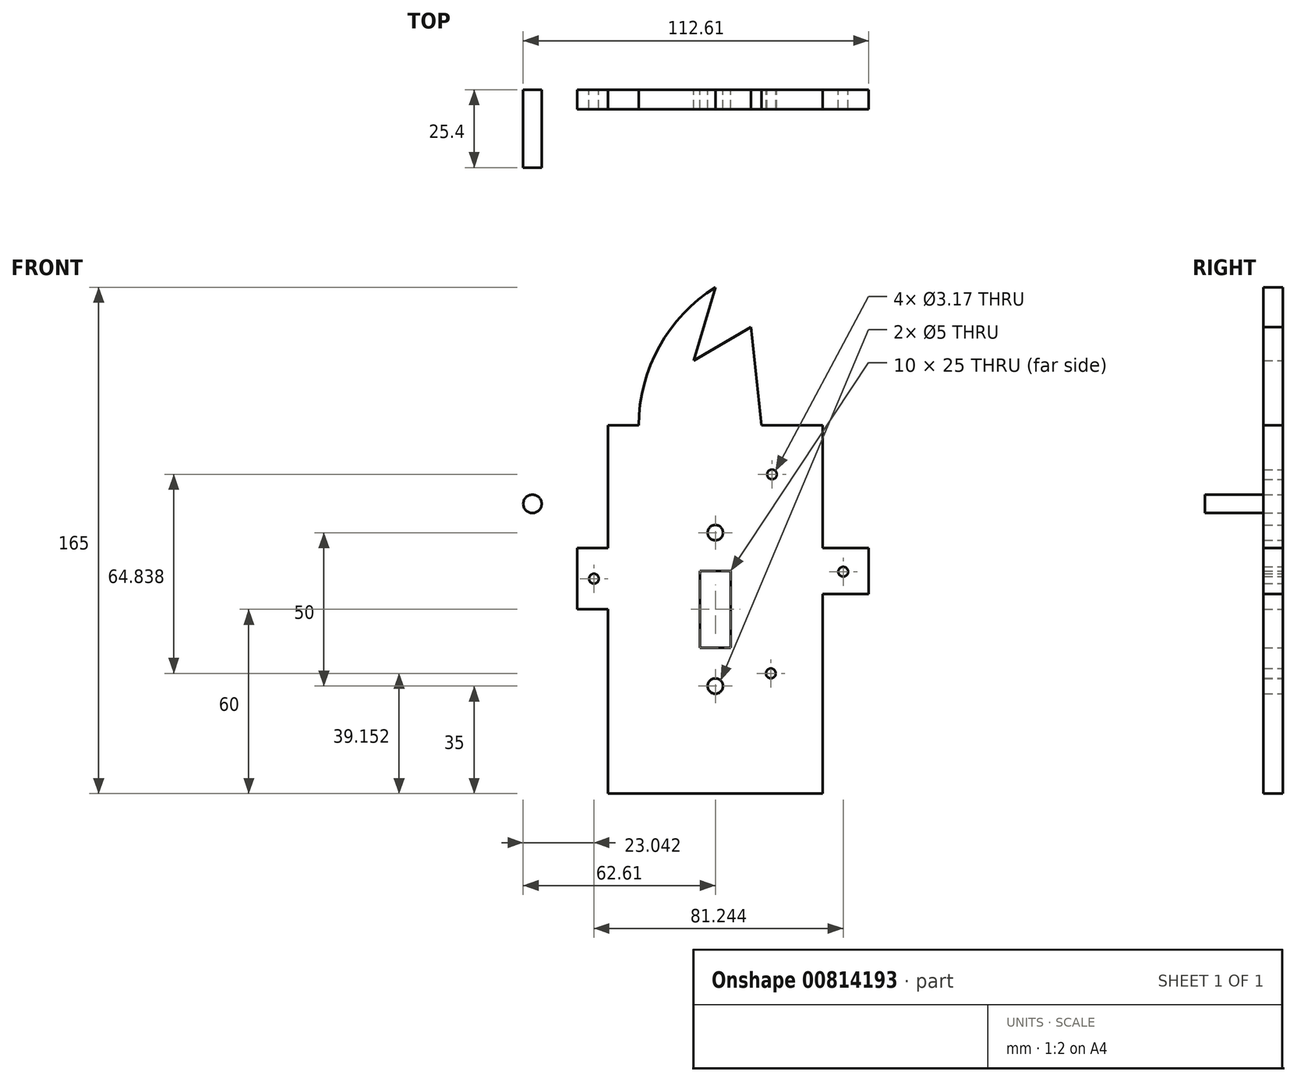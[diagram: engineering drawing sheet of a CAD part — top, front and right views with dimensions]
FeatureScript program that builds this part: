
annotation { "Feature Type Name" : "Feature", "Feature Type Description" : "" }
export const myFeature = defineFeature(function(context is Context, id is Id, definition is map)
    precondition{}
    {
        {
            var Q0;
            Q0=qCreatedBy(makeId("Front.planeOp"),FACE);
            var sketch = newSketch(context, id + "F0", { "sketchPlane" : qUnion([Q0])});
            skLineSegment(sketch, "E0.bottom", {"start": v(35, -60) * mm, "end": v(-35, -60) * mm});
            skPoint(sketch, "E0.middle", {"position": v(0, 0) * mm});
            skPoint(sketch, "E1", {"position": v(-25, 60) * mm});
            skArc(sketch, "E2", {"start": v(0, 105) * mm, "mid": v(-18.24, 85.69) * mm, "end": v(-25, 60) * mm});
            skPoint(sketch, "E3", {"position": v(15, 60) * mm});
            skLineSegment(sketch, "E4", {"start": v(0, 105) * mm, "end": v(-7.06, 81.1) * mm});
            skLineSegment(sketch, "E5", {"start": v(-7.06, 81.1) * mm, "end": v(4.65, 87.98) * mm});
            skLineSegment(sketch, "E6", {"start": v(4.65, 87.98) * mm, "end": v(11.62, 92.07) * mm});
            skLineSegment(sketch, "E7", {"start": v(11.62, 92.07) * mm, "end": v(15, 60) * mm});
            skLineSegment(sketch, "E8.bottom", {"start": v(-5, -12.5) * mm, "end": v(5, -12.5) * mm});
            skLineSegment(sketch, "E8.top", {"start": v(-5, 12.5) * mm, "end": v(5, 12.5) * mm});
            skLineSegment(sketch, "E8.left", {"start": v(-5, -12.5) * mm, "end": v(-5, 12.5) * mm});
            skLineSegment(sketch, "E8.right", {"start": v(5, -12.5) * mm, "end": v(5, 12.5) * mm});
            skCircle(sketch, "E9", {"center": v(0, -25) * mm, "radius": 2.5 * mm});
            skCircle(sketch, "E10", {"center": v(0, 25) * mm, "radius": 2.5 * mm});
            skPoint(sketch, "E11", {"position": v(-35, 20) * mm});
            skLineSegment(sketch, "E12.bottom", {"start": v(-35, 20) * mm, "end": v(-45, 20) * mm});
            skLineSegment(sketch, "E12.top", {"start": v(-35, 0) * mm, "end": v(-45, 0) * mm});
            skLineSegment(sketch, "E12.right", {"start": v(-45, 20) * mm, "end": v(-45, 0) * mm});
            skPoint(sketch, "E13", {"position": v(35, 20) * mm});
            skLineSegment(sketch, "E14.bottom", {"start": v(35, 20) * mm, "end": v(50, 20) * mm});
            skLineSegment(sketch, "E14.top", {"start": v(35, 5) * mm, "end": v(50, 5) * mm});
            skLineSegment(sketch, "E14.right", {"start": v(50, 20) * mm, "end": v(50, 5) * mm});
            skCircle(sketch, "E15", {"center": v(41.68, 12.27) * mm, "radius": 1.59 * mm});
            skCircle(sketch, "E16", {"center": v(-39.57, 10) * mm, "radius": 1.59 * mm});
            skPoint(sketch, "E16.centerSnap0", {"position": v(-45, 10) * mm});
            skCircle(sketch, "E17", {"center": v(-59.61, 34.39) * mm, "radius": 3 * mm});
            skPoint(sketch, "E18", {"position": v(20.53, -42.5) * mm});
            skLineSegment(sketch, "E19", {"start": v(-35, 60) * mm, "end": v(-25, 60) * mm});
            skLineSegment(sketch, "E20", {"start": v(15, 60) * mm, "end": v(35, 60) * mm});
            skLineSegment(sketch, "E21", {"start": v(-35, 60) * mm, "end": v(-35, 20) * mm});
            skLineSegment(sketch, "E22", {"start": v(-35, 0) * mm, "end": v(-35, -60) * mm});
            skLineSegment(sketch, "E23", {"start": v(35, 60) * mm, "end": v(35, 20) * mm});
            skLineSegment(sketch, "E24", {"start": v(35, 5) * mm, "end": v(35, -60) * mm});
            skCircle(sketch, "E25", {"center": v(18.1, -20.85) * mm, "radius": 1.59 * mm});
            skCircle(sketch, "E26", {"center": v(18.47, 44) * mm, "radius": 1.59 * mm});
            skSolve(sketch);
        }
        {
            var Q0;
            {var subQ0=sQuery(id+"F0.wireOp",EDGE,"E2");Q0=makeQuery(id+"F0.imprint","IMPRINT",FACE,{"disambiguationData":[TD([[makeQuery(id+"F0.imprint","IMPRINT",EDGE,{"derivedFrom":subQ0}),1.0]])]});}
            var Q1;
            Q1=makeQuery(id+"F0.imprint","IMPRINT",FACE,{"disambiguationData":[TD([[makeQuery(id+"F0.imprint","IMPRINT",EDGE,{"derivedFrom":sQuery(id+"F0.wireOp",EDGE,"E0.bottom")}),-1.0]])]});
            var Q2;
            Q2=makeQuery(id+"F0.imprint","IMPRINT",FACE,{"disambiguationData":[TD([[makeQuery(id+"F0.imprint","IMPRINT",EDGE,{"derivedFrom":sQuery(id+"F0.wireOp",EDGE,"E12.bottom")}),1.0]])]});
            var Q3;
            Q3=makeQuery(id+"F0.imprint","IMPRINT",FACE,{"disambiguationData":[TD([[makeQuery(id+"F0.imprint","IMPRINT",EDGE,{"derivedFrom":sQuery(id+"F0.wireOp",EDGE,"E14.bottom")}),-1.0]])]});
            extrude(context, id + "F1", {"entities" : qUnion([Q0, Q1, Q2, Q3]), "depth" : 6.35 * mm, "offsetDistance" : 25.4 * mm});
        }
        {
            var Q0;
            Q0=makeQuery(id+"F0.imprint","IMPRINT",FACE,{"disambiguationData":[TD([[makeQuery(id+"F0.imprint","IMPRINT",EDGE,{"derivedFrom":sQuery(id+"F0.wireOp",EDGE,"E17")}),1.0]])]});
            extrude(context, id + "F2", {"entities" : qUnion([Q0]), "depth" : 25.4 * mm, "offsetDistance" : 25.4 * mm});
        }
    });
